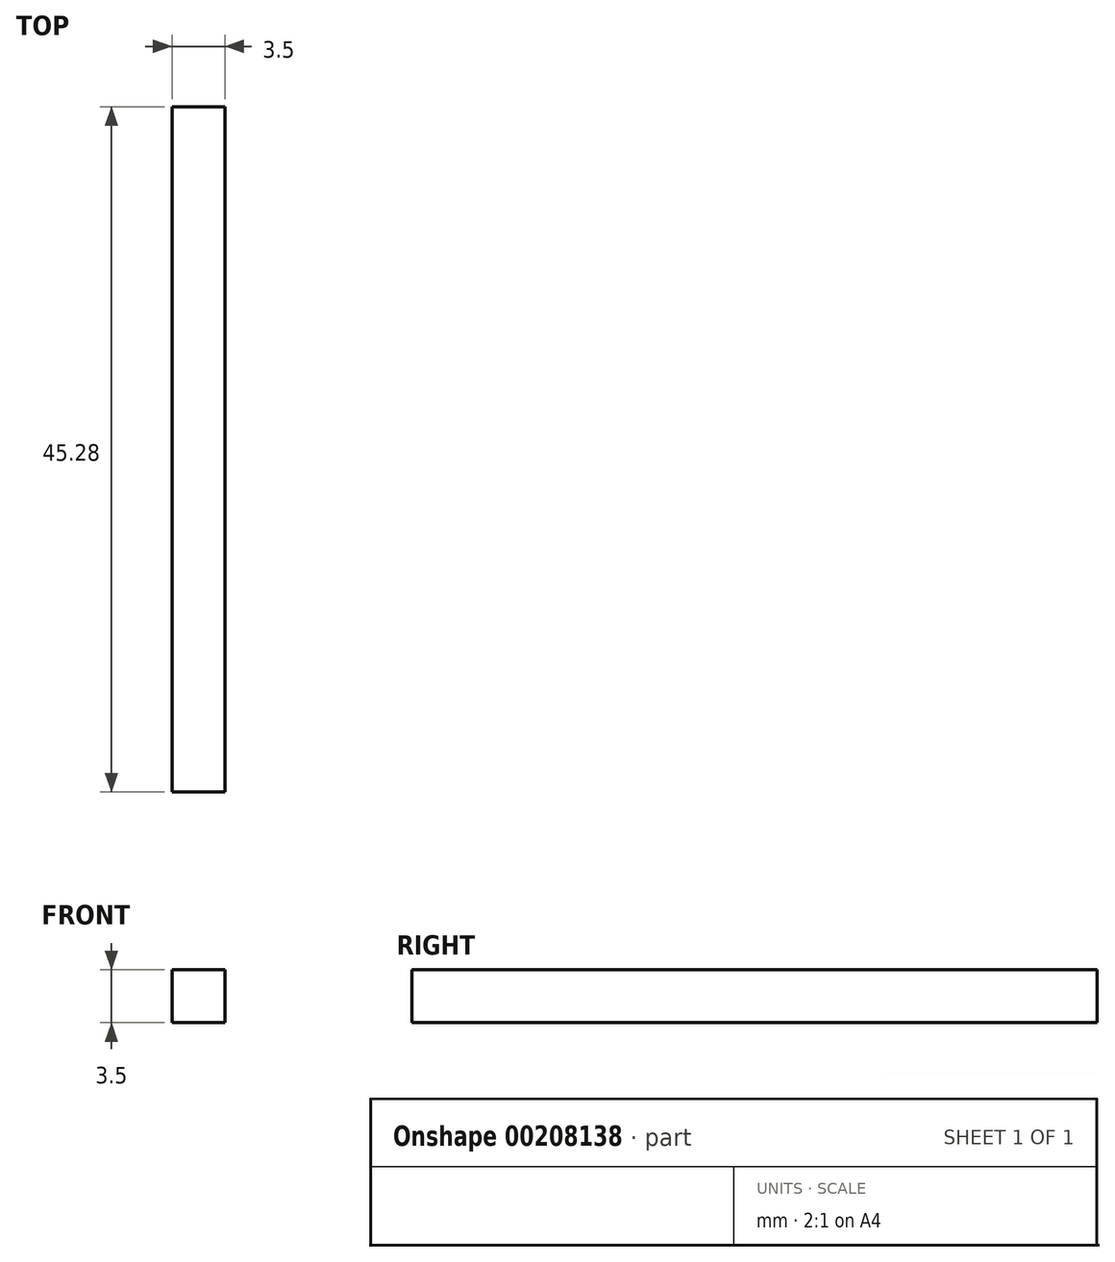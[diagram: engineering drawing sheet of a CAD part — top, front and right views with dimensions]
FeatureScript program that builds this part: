
annotation { "Feature Type Name" : "Feature", "Feature Type Description" : "" }
export const myFeature = defineFeature(function(context is Context, id is Id, definition is map)
    precondition{}
    {
        {
            var Q0;
            Q0=qCreatedBy(makeId("Top.planeOp"),FACE);
            var sketch = newSketch(context, id + "F0", { "sketchPlane" : qUnion([Q0])});
            skLineSegment(sketch, "E0.bottom", {"start": v(-1.75, 22.64) * mm, "end": v(1.75, 22.64) * mm});
            skLineSegment(sketch, "E0.top", {"start": v(-1.75, -22.64) * mm, "end": v(1.75, -22.64) * mm});
            skLineSegment(sketch, "E0.left", {"start": v(-1.75, 22.64) * mm, "end": v(-1.75, -22.64) * mm});
            skLineSegment(sketch, "E0.right", {"start": v(1.75, 22.64) * mm, "end": v(1.75, -22.64) * mm});
            skPoint(sketch, "E0.middle", {"position": v(0, 0) * mm});
            skSolve(sketch);
        }
        {
            var Q0;
            Q0 = qSketchRegion(id + "F0", true);
            extrude(context, id + "F1", {"entities" : qUnion([Q0]), "depth" : 3.5 * mm});
        }
    });
